# Revit family: LBTYP008
name_source: partatom
category: Furniture
units: mm (PartAtom-declared; Revit-internal decimal feet)

## family parameters
Always vertical = Yes
Cut with Voids When Loaded = No
OmniClass Number = 23.40.20.00
OmniClass Title = General Furniture and Specialties
Render Appearance Source = Family Geometry
Room Calculation Point = No
Shared = No
Work Plane-Based = No

## types (1)
- LBTYP008
    Cost = 42182 $
    Default Elevation = 0 mm  [stored 0 ft]
    Description = 4 x Volker Cube w/Casters - 18x18x18, 3 x Volker Cube w/Casters - 18x18x18, 2 x LB LOUNGE LEDGE KIT 13"d X 66"w, 2 x LB LOUNGE, CORNER, 50 TALL, SOLID BASE, REAR OVERLAY, LEFT, 1 x LB Lounge 2 Seat 42H X 48W X 30 Open Base, 1 x LB Lounge 3 Seat 42H X 66W X 30 Open Base, 1 x LB LOUNGE 2 SEAT 42"H X 48"W X 30" SOLID BASE, 1 x LB LOUNGE 3 SEAT 42"H X 66"W X 30" SOLID BASE, 1 x COLLAB TBL, D-TOP, 2mm, 36Dx66Wx29H, DISC, 1 x TBL, PBL, KNF, 30Dx16H, DISC, GLD, 1 x TBL, PEB, KNF, 30Dx60Wx16H, DISC, GLD, 1 x Calibrate Dry Planter 42Hx42Wx12D, 2 x Calibrate Dry Planter 42Hx48Wx12D, 2 x Calibrate Dry Planter 50Hx30Wx12D, 1 x Collaborative Table Wall Mount Kit (4 Black Brackets)
    Exported From CET Designer = Yes
    Manufacturer = AIS
    Model = F-CUBE181818
    Show LBTYP008 = Yes
    VisibilityIndex = 0

note: [stored X ft] marks values corroborated as IEEE doubles in the binary element streams (Revit-internal decimal feet)

## geometry (parser evidence)
native form markers: Sweep x2
no freeform markers — native parametric forms only
